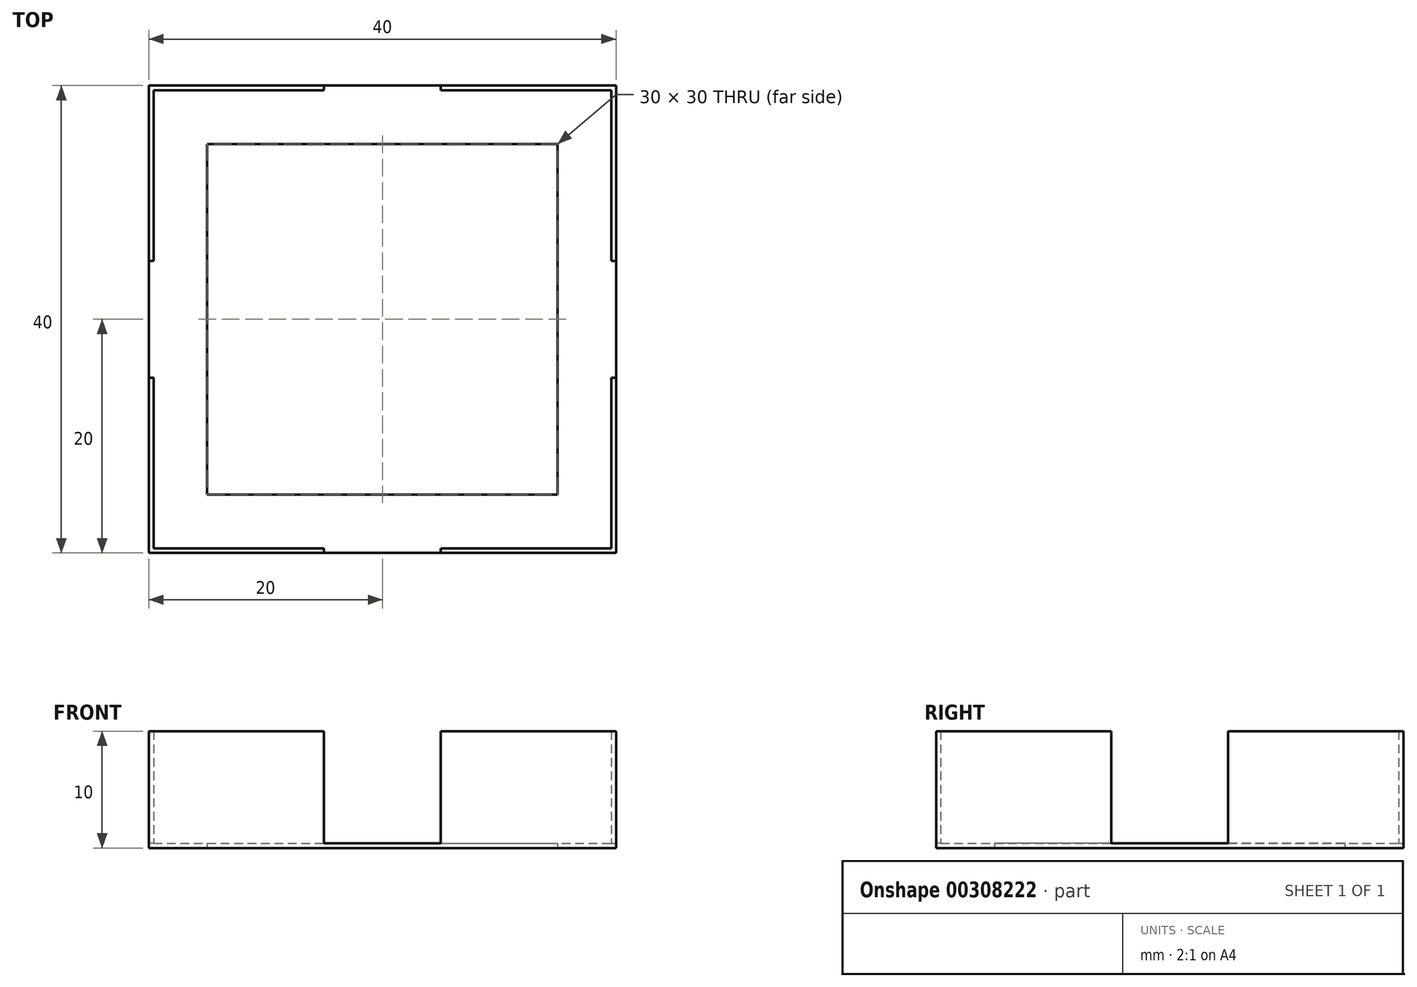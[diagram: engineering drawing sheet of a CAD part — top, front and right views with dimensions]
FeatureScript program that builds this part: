
annotation { "Feature Type Name" : "Feature", "Feature Type Description" : "" }
export const myFeature = defineFeature(function(context is Context, id is Id, definition is map)
    precondition{}
    {
        {
            assignVariable(context, id + "F0", {"name" : "thick_bottom", "anyValue" : .4});
        }
        {
            var Q0;
            Q0=qCreatedBy(makeId("Top.planeOp"),FACE);
            var sketch = newSketch(context, id + "F1", { "sketchPlane" : qUnion([Q0])});
            skLineSegment(sketch, "E0.bottom", {"start": v(-20, 20) * mm, "end": v(-5, 20) * mm});
            skLineSegment(sketch, "E0.top", {"start": v(-20, -20) * mm, "end": v(-5, -20) * mm});
            skLineSegment(sketch, "E0.left", {"start": v(-20, 20) * mm, "end": v(-20, 5) * mm});
            skLineSegment(sketch, "E0.right", {"start": v(20, 20) * mm, "end": v(20, 5) * mm});
            skPoint(sketch, "E0.middle", {"position": v(0, 0) * mm});
            skLineSegment(sketch, "E1", {"start": v(20, -5) * mm, "end": v(20, -20) * mm});
            skLineSegment(sketch, "E2", {"start": v(20, 5) * mm, "end": v(20, -5) * mm});
            skLineSegment(sketch, "E3", {"start": v(5, 20) * mm, "end": v(20, 20) * mm});
            skLineSegment(sketch, "E4", {"start": v(-5, 20) * mm, "end": v(5, 20) * mm});
            skLineSegment(sketch, "E5", {"start": v(-20, 5) * mm, "end": v(-20, -5) * mm});
            skLineSegment(sketch, "E6", {"start": v(-20, -5) * mm, "end": v(-20, -20) * mm});
            skLineSegment(sketch, "E7", {"start": v(-5, -20) * mm, "end": v(5, -20) * mm});
            skLineSegment(sketch, "E8", {"start": v(5, -20) * mm, "end": v(20, -20) * mm});
            skLineSegment(sketch, "E9", {"start": v(20, -5) * mm, "end": v(19.6, -5) * mm});
            skLineSegment(sketch, "E10", {"start": v(19.6, -5) * mm, "end": v(19.6, -19.6) * mm});
            skLineSegment(sketch, "E11", {"start": v(19.6, -19.6) * mm, "end": v(5, -19.6) * mm});
            skLineSegment(sketch, "E12", {"start": v(5, -19.6) * mm, "end": v(5, -20) * mm});
            skLineSegment(sketch, "E13", {"start": v(-5, -20) * mm, "end": v(-5, -19.6) * mm});
            skLineSegment(sketch, "E14", {"start": v(-5, -19.6) * mm, "end": v(-19.6, -19.6) * mm});
            skLineSegment(sketch, "E15", {"start": v(-19.6, -19.6) * mm, "end": v(-19.6, -5) * mm});
            skLineSegment(sketch, "E16", {"start": v(-19.6, -5) * mm, "end": v(-20, -5) * mm});
            skLineSegment(sketch, "E17", {"start": v(-20, 5) * mm, "end": v(-19.6, 5) * mm});
            skLineSegment(sketch, "E18", {"start": v(-19.6, 5) * mm, "end": v(-19.6, 19.6) * mm});
            skLineSegment(sketch, "E19", {"start": v(-19.6, 19.6) * mm, "end": v(-5, 19.6) * mm});
            skLineSegment(sketch, "E20", {"start": v(-5, 19.6) * mm, "end": v(-5, 20) * mm});
            skLineSegment(sketch, "E21", {"start": v(5, 20) * mm, "end": v(5, 19.6) * mm});
            skLineSegment(sketch, "E22", {"start": v(5, 19.6) * mm, "end": v(19.6, 19.6) * mm});
            skLineSegment(sketch, "E23", {"start": v(19.6, 19.6) * mm, "end": v(19.6, 5) * mm});
            skLineSegment(sketch, "E24", {"start": v(19.6, 5) * mm, "end": v(20, 5) * mm});
            skLineSegment(sketch, "E25.bottom", {"start": v(-15, 15) * mm, "end": v(15, 15) * mm});
            skLineSegment(sketch, "E25.top", {"start": v(-15, -15) * mm, "end": v(15, -15) * mm});
            skLineSegment(sketch, "E25.left", {"start": v(-15, 15) * mm, "end": v(-15, -15) * mm});
            skLineSegment(sketch, "E25.right", {"start": v(15, 15) * mm, "end": v(15, -15) * mm});
            skSolve(sketch);
        }
        {
            var Q0;
            Q0=makeQuery(id+"F1.imprint","IMPRINT",FACE,{"disambiguationData":[TD([[makeQuery(id+"F1.imprint","IMPRINT",EDGE,{"derivedFrom":sQuery(id+"F1.wireOp",EDGE,"E0.bottom")}),-1.0]])]});
            var Q1;
            Q1=makeQuery(id+"F1.imprint","IMPRINT",FACE,{"disambiguationData":[TD([[makeQuery(id+"F1.imprint","IMPRINT",EDGE,{"derivedFrom":sQuery(id+"F1.wireOp",EDGE,"E0.right")}),-1.0]])]});
            var Q2;
            Q2=makeQuery(id+"F1.imprint","IMPRINT",FACE,{"disambiguationData":[TD([[makeQuery(id+"F1.imprint","IMPRINT",EDGE,{"derivedFrom":sQuery(id+"F1.wireOp",EDGE,"E2")}),-1.0]])]});
            var Q3;
            Q3=makeQuery(id+"F1.imprint","IMPRINT",FACE,{"disambiguationData":[TD([[makeQuery(id+"F1.imprint","IMPRINT",EDGE,{"derivedFrom":sQuery(id+"F1.wireOp",EDGE,"E1")}),-1.0]])]});
            var Q4;
            Q4=makeQuery(id+"F1.imprint","IMPRINT",FACE,{"disambiguationData":[TD([[makeQuery(id+"F1.imprint","IMPRINT",EDGE,{"derivedFrom":sQuery(id+"F1.wireOp",EDGE,"E0.top")}),1.0]])]});
            extrude(context, id + "F2", {"entities" : qUnion([Q0, Q1, Q2, Q3, Q4]), "depth" : (getVariable(context, 'thick_bottom')) * mm, "offsetDistance" : 25 * mm});
        }
        {
            var Q0;
            Q0=makeQuery(id+"F1.imprint","IMPRINT",FACE,{"disambiguationData":[TD([[makeQuery(id+"F1.imprint","IMPRINT",EDGE,{"derivedFrom":sQuery(id+"F1.wireOp",EDGE,"E1")}),-1.0]])]});
            var Q1;
            Q1=makeQuery(id+"F1.imprint","IMPRINT",FACE,{"disambiguationData":[TD([[makeQuery(id+"F1.imprint","IMPRINT",EDGE,{"derivedFrom":sQuery(id+"F1.wireOp",EDGE,"E0.top")}),1.0]])]});
            var Q2;
            Q2=makeQuery(id+"F1.imprint","IMPRINT",FACE,{"disambiguationData":[TD([[makeQuery(id+"F1.imprint","IMPRINT",EDGE,{"derivedFrom":sQuery(id+"F1.wireOp",EDGE,"E0.right")}),-1.0]])]});
            var Q3;
            Q3=makeQuery(id+"F1.imprint","IMPRINT",FACE,{"disambiguationData":[TD([[makeQuery(id+"F1.imprint","IMPRINT",EDGE,{"derivedFrom":sQuery(id+"F1.wireOp",EDGE,"E0.bottom")}),-1.0]])]});
            extrude(context, id + "F3", {"entities" : qUnion([Q0, Q1, Q2, Q3]), "operationType" : NewBodyOperationType.ADD, "depth" : 10 * mm, "offsetDistance" : 25 * mm});
        }
    });
